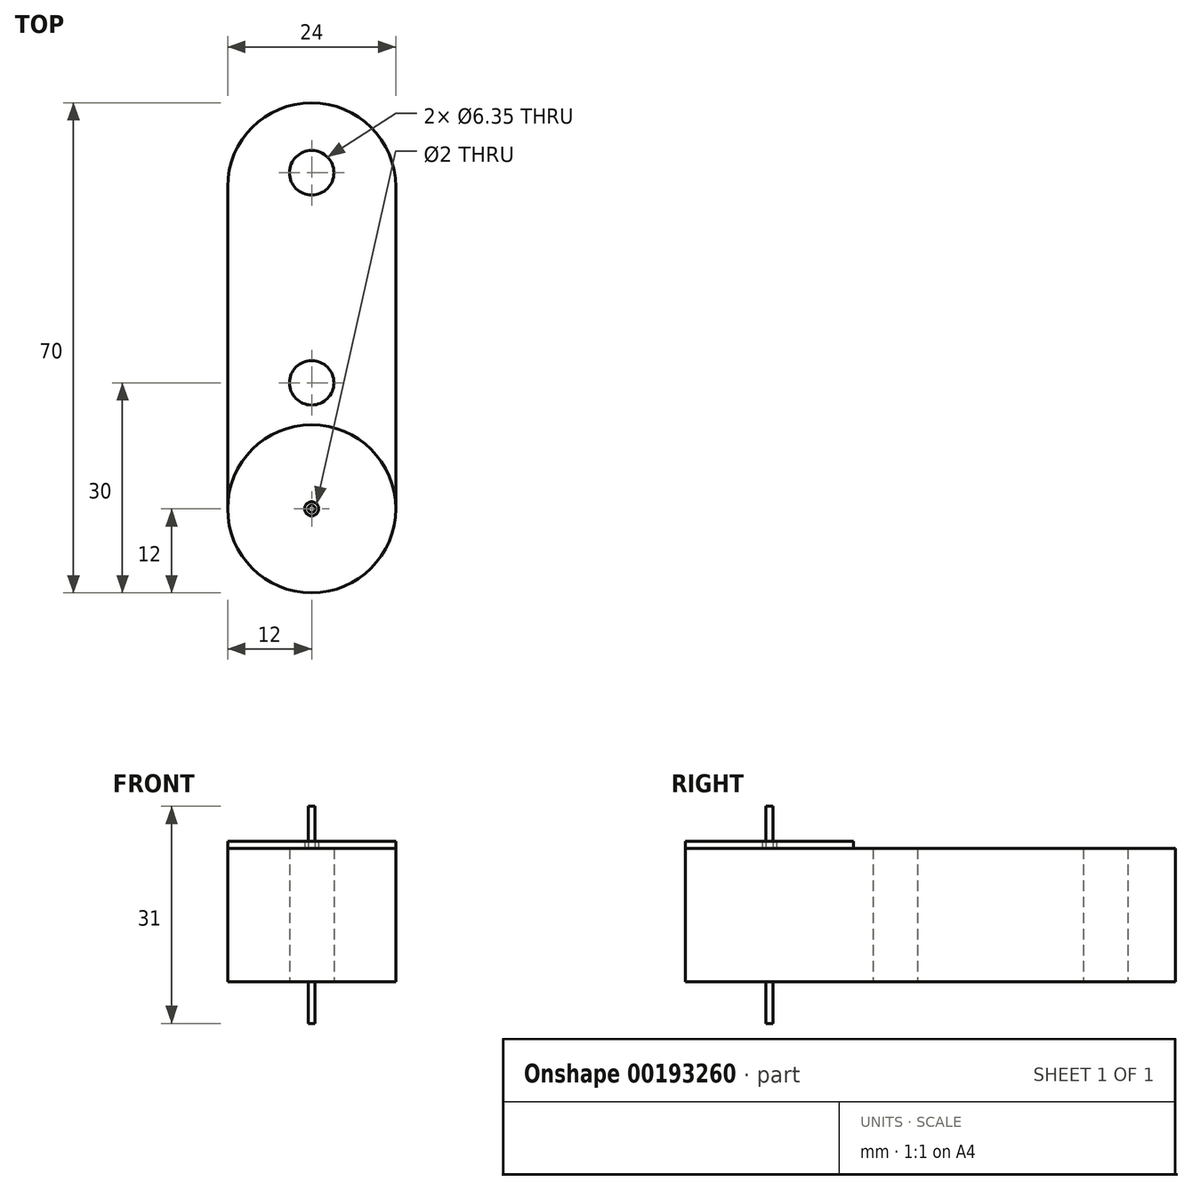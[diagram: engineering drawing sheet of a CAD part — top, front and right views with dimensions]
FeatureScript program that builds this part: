
annotation { "Feature Type Name" : "Feature", "Feature Type Description" : "" }
export const myFeature = defineFeature(function(context is Context, id is Id, definition is map)
    precondition{}
    {
        {
            var Q0;
            Q0=qCreatedBy(makeId("Top.planeOp"),FACE);
            var sketch = newSketch(context, id + "F0", { "sketchPlane" : qUnion([Q0])});
            skLineSegment(sketch, "E0.bottom", {"start": v(12, 35) * mm, "end": v(-12, 35) * mm});
            skLineSegment(sketch, "E0.top", {"start": v(12, -35) * mm, "end": v(-12, -35) * mm});
            skLineSegment(sketch, "E0.left", {"start": v(12, 35) * mm, "end": v(12, -35) * mm});
            skLineSegment(sketch, "E0.right", {"start": v(-12, 35) * mm, "end": v(-12, -35) * mm});
            skPoint(sketch, "E0.middle", {"position": v(0, 0) * mm});
            skLineSegment(sketch, "E1", {"start": v(0, 35) * mm, "end": v(0, 25) * mm});
            skPoint(sketch, "E1.endSnap0", {"position": v(0, 35) * mm});
            skCircle(sketch, "E2", {"center": v(0, 25) * mm, "radius": 3.17 * mm});
            skLineSegment(sketch, "E3", {"start": v(0, 25) * mm, "end": v(0, -5) * mm});
            skCircle(sketch, "E4", {"center": v(0, -5) * mm, "radius": 3.17 * mm});
            skCircle(sketch, "E5", {"center": v(0, -23) * mm, "radius": 0.5 * mm});
            skLineSegment(sketch, "E6", {"start": v(0, -23) * mm, "end": v(0, -35) * mm});
            skLineSegment(sketch, "E7", {"start": v(0, -5) * mm, "end": v(0, -23) * mm});
            skSolve(sketch);
        }
        {
            var Q0;
            Q0 = qSketchRegion(id + "F0", true);
            extrude(context, id + "F1", {"entities" : qUnion([Q0]), "depth" : 19.05 * mm});
        }
        {
            var Q0;
            Q0=makeQuery(id+"F1.opExtrude","CAP_FACE",FACE,{"disambiguationData":[OSD([sQuery(id+"F0.wireOp",EDGE,"E0.bottom"),sQuery(id+"F0.wireOp",EDGE,"E0.top"),sQuery(id+"F0.wireOp",EDGE,"E0.left"),sQuery(id+"F0.wireOp",EDGE,"E0.right"),sQuery(id+"F0.wireOp",EDGE,"E2"),sQuery(id+"F0.wireOp",EDGE,"E4")])],"isStart":false});
            var sketch = newSketch(context, id + "F2", { "sketchPlane" : qUnion([Q0])});
            skCircle(sketch, "E8", {"center": v(0, -23) * mm, "radius": 1 * mm});
            skCircle(sketch, "E9", {"center": v(0, -23) * mm, "radius": 12 * mm});
            skSolve(sketch);
        }
        {
            var Q0;
            Q0=makeQuery(id+"F2.imprint","IMPRINT",FACE,{"disambiguationData":[TD([[makeQuery(id+"F2.imprint","IMPRINT",EDGE,{"derivedFrom":sQuery(id+"F2.wireOp",EDGE,"E8")}),-1.0]])]});
            extrude(context, id + "F3", {"entities" : qUnion([Q0]), "depth" : 1 * mm});
        }
        {
            var Q0;
            Q0=makeQuery(id+"F1.opExtrude","CAP_FACE",FACE,{"disambiguationData":[OSD([sQuery(id+"F0.wireOp",EDGE,"E0.bottom"),sQuery(id+"F0.wireOp",EDGE,"E0.top"),sQuery(id+"F0.wireOp",EDGE,"E0.left"),sQuery(id+"F0.wireOp",EDGE,"E0.right"),sQuery(id+"F0.wireOp",EDGE,"E2"),sQuery(id+"F0.wireOp",EDGE,"E4"),sQuery(id+"F0.wireOp",EDGE,"E5")])],"isStart":false});
            var sketch = newSketch(context, id + "F4", { "sketchPlane" : qUnion([Q0])});
            skLineSegment(sketch, "E10", {"start": v(0, -23) * mm, "end": v(0, -23.5) * mm});
            skCircle(sketch, "E11", {"center": v(0, -23) * mm, "radius": 0.5 * mm});
            skSolve(sketch);
        }
        {
            var Q0;
            Q0 = qSketchRegion(id + "F4", true);
            extrude(context, id + "F5", {"entities" : qUnion([Q0]), "operationType" : NewBodyOperationType.ADD, "depth" : 6 * mm, "hasSecondDirection" : true, "secondDirectionOppositeDirection" : true, "secondDirectionDepth" : 25 * mm});
        }
        {
            var Q0;
            Q0=makeQuery(id+"F1.opExtrude","SWEPT_EDGE",EDGE,{"disambiguationData":[OSD([sQuery(id+"F0.wireOp",EDGE,"E0.bottom"),sQuery(id+"F0.wireOp",EDGE,"E0.right")])]});
            var Q1;
            Q1=makeQuery(id+"F1.opExtrude","SWEPT_EDGE",EDGE,{"disambiguationData":[OSD([sQuery(id+"F0.wireOp",EDGE,"E0.bottom"),sQuery(id+"F0.wireOp",EDGE,"E0.left")])]});
            var Q2;
            Q2=makeQuery(id+"F1.opExtrude","SWEPT_EDGE",EDGE,{"disambiguationData":[OSD([sQuery(id+"F0.wireOp",EDGE,"E0.top"),sQuery(id+"F0.wireOp",EDGE,"E0.left")])]});
            var Q3;
            Q3=makeQuery(id+"F1.opExtrude","SWEPT_EDGE",EDGE,{"disambiguationData":[OSD([sQuery(id+"F0.wireOp",EDGE,"E0.top"),sQuery(id+"F0.wireOp",EDGE,"E0.right")])]});
            fillet(context, id + "F6", {"entities" : qUnion([Q0, Q1, Q2, Q3]), "radius" : 12 * mm, "tangentPropagation" : true, "allowEdgeOverflow" : false});
        }
    });
